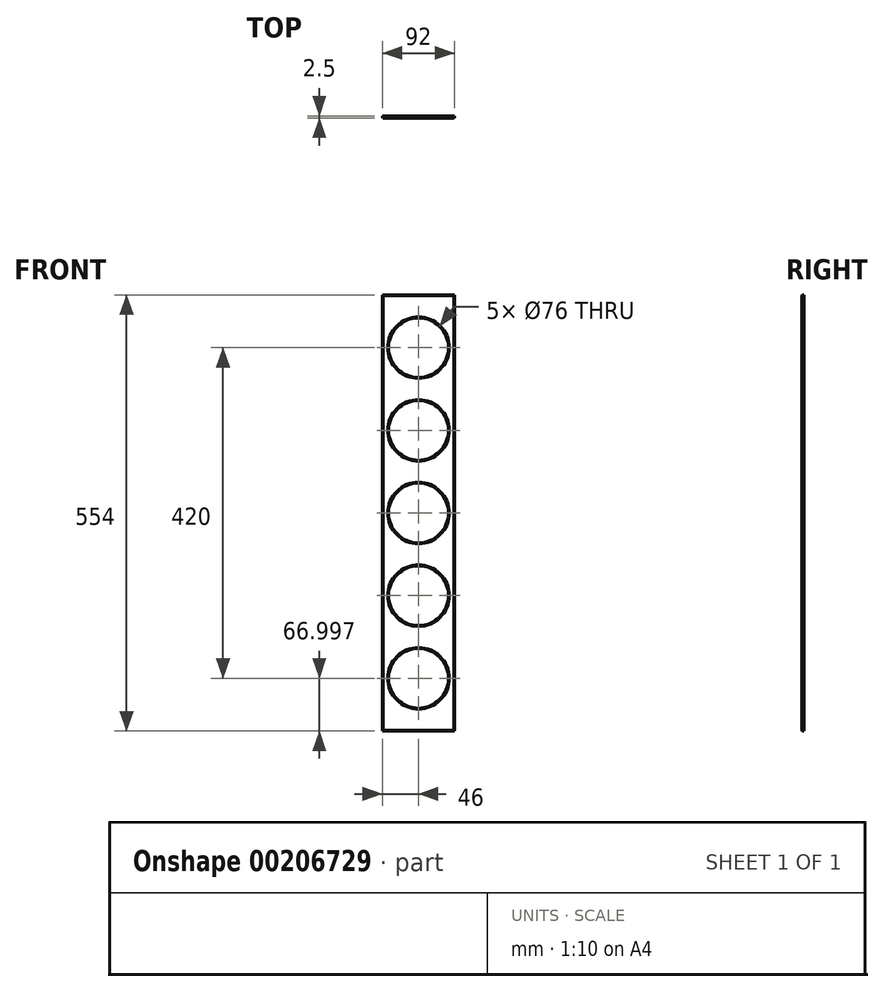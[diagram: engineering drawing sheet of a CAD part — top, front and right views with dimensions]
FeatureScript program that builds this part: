
annotation { "Feature Type Name" : "Feature", "Feature Type Description" : "" }
export const myFeature = defineFeature(function(context is Context, id is Id, definition is map)
    precondition{}
    {
        {
            var Q0;
            Q0=qCreatedBy(makeId("Front.planeOp"),FACE);
            var sketch = newSketch(context, id + "F0", { "sketchPlane" : qUnion([Q0])});
            skLineSegment(sketch, "E0.bottom", {"start": v(-48.4, 452) * mm, "end": v(43.6, 452) * mm});
            skLineSegment(sketch, "E0.top", {"start": v(-48.4, -102) * mm, "end": v(43.6, -102) * mm});
            skLineSegment(sketch, "E0.left", {"start": v(-48.4, 452) * mm, "end": v(-48.4, -102) * mm});
            skLineSegment(sketch, "E0.right", {"start": v(43.6, 452) * mm, "end": v(43.6, -102) * mm});
            skLineSegment(sketch, "E1", {"start": v(-2.4, 452) * mm, "end": v(-2.4, -102) * mm, "construction": true});
            skCircle(sketch, "E2", {"center": v(-2.4, 385) * mm, "radius": 38 * mm});
            skCircle(sketch, "E3.0.1.0", {"center": v(-2.4, 280) * mm, "radius": 38 * mm});
            skCircle(sketch, "E3.0.2.0", {"center": v(-2.4, 175) * mm, "radius": 38 * mm});
            skCircle(sketch, "E3.0.3.0", {"center": v(-2.4, 70) * mm, "radius": 38 * mm});
            skCircle(sketch, "E3.0.4.0", {"center": v(-2.4, -35) * mm, "radius": 38 * mm});
            skLineSegment(sketch, "E3.direction1", {"start": v(-2.4, 385) * mm, "end": v(22.6, 385) * mm, "construction": true});
            skLineSegment(sketch, "E3.direction2", {"start": v(-2.4, 385) * mm, "end": v(-2.4, 280) * mm, "construction": true});
            skSolve(sketch);
        }
        {
            var Q0;
            Q0=makeQuery(id+"F0.imprint","IMPRINT",FACE,{"disambiguationData":[TD([[makeQuery(id+"F0.imprint","IMPRINT",EDGE,{"derivedFrom":sQuery(id+"F0.wireOp",EDGE,"E0.bottom")}),-1.0]])]});
            extrude(context, id + "F1", {"entities" : qUnion([Q0]), "depth" : 2.5 * mm});
        }
        {
            var Q0;
            Q0=makeQuery(id+"F1.opExtrude","CAP_FACE",FACE,{"disambiguationData":[OSD([sQuery(id+"F0.wireOp",EDGE,"E0.bottom"),sQuery(id+"F0.wireOp",EDGE,"E0.top"),sQuery(id+"F0.wireOp",EDGE,"E0.left"),sQuery(id+"F0.wireOp",EDGE,"E0.right"),sQuery(id+"F0.wireOp",EDGE,"E2"),sQuery(id+"F0.wireOp",EDGE,"E3.0.1.0"),sQuery(id+"F0.wireOp",EDGE,"E3.0.2.0"),sQuery(id+"F0.wireOp",EDGE,"E3.0.3.0"),sQuery(id+"F0.wireOp",EDGE,"E3.0.4.0")])],"isStart":false});
            chamfer(context, id + "F2", {"entities" : qUnion([Q0]), "width" : 1 * mm, "tangentPropagation" : true});
        }
    });
